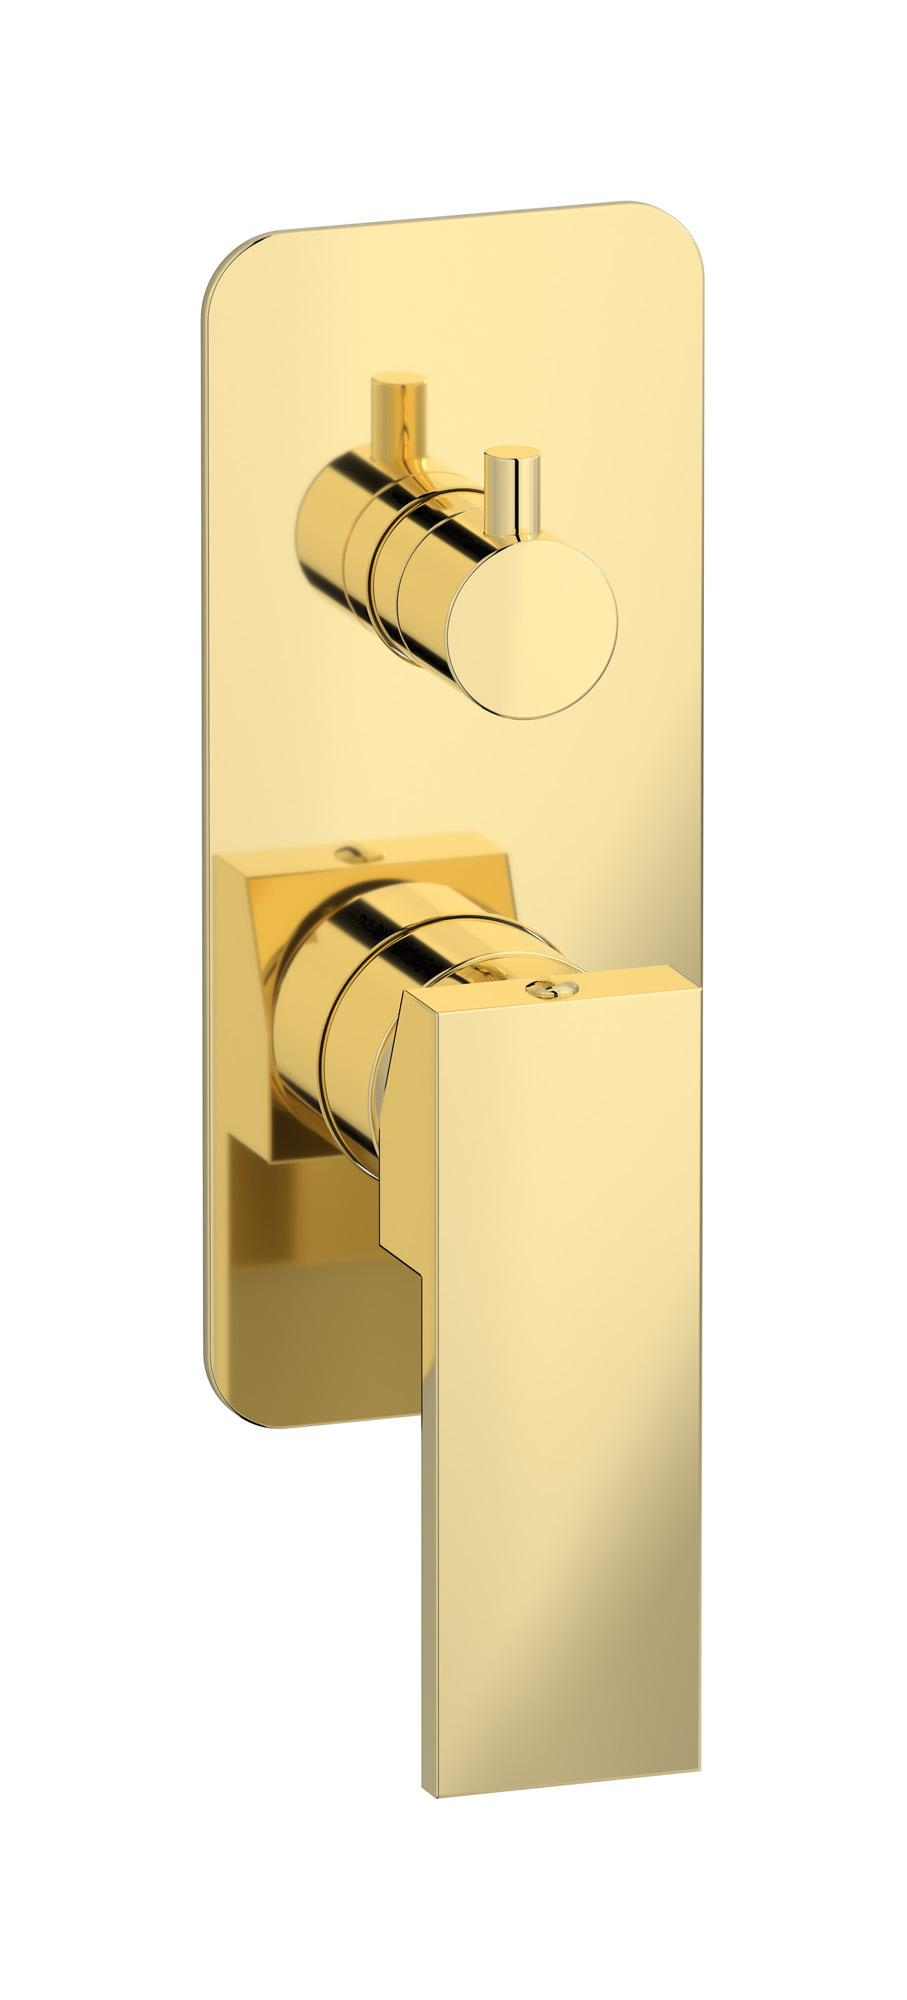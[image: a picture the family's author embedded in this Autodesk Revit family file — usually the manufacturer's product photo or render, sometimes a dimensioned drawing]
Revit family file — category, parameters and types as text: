
# Revit family: RU312
name_source: partatom
category: Apparecchi idraulici
units: mm (PartAtom-declared; Revit-internal decimal feet)

## family parameters
Basato su piano di lavoro = No
Condiviso = No
Mantieni orientamento annotazione = No
Numero OmniClass = 23.45.55.17
Punto di calcolo locali = No
Quota connettore circolare = Usa diametro
Sempre verticale = Sì
Taglio con vuoti quando caricato = No
Tipo di parte = Normale
Titolo OmniClass = Mixing Faucets

## types (12) — shared parameters
Cold water inlet = 10 mm  [stored 0.0328084 ft]
Commenti sul tipo = Exposed parts for manual wall mixer with three ways diverter
Connessione CW = No
Connessione HW = No
Connessione di scarico = No
Connessione di ventilazione = No
Descrizione = Exposed parts for manual wall mixer with three ways diverter
Hot water inlet = 10 mm  [stored 0.0328084 ft]
Produttore = IB Rubinetterie S.p.A.
URL = https://www.weareib.it
zero-valued in all types: Prospetto di default

## per-type parameters (varying)
| type | Finishes surface | Immagine tipo | Modello |
| Matt White | IB_matt white | RU312BO.jpg | RU312BO |
| Chrome | IB_Chrome | RU312CC.jpg | RU312CC |
| Black Chrome | IB_Black chrome | RU312CF.jpg | RU312CF |
| Brushed Black Chrome | IB_Brushed black chrome | RU312CS.jpg | RU312CS |
| Pale Gold | IB_Pale gold | RU312II.jpg | RU312II |
| Brushed Pale Gold | IB_brushed pale gold | RU312IS.jpg | RU312IS |
| Matt Black | IB_matt black | RU312NP.jpg | RU312NP |
| Gold | IB_gold | RU312OO.jpg | RU312OO |
| Brushed Gold | IB_brushed gold | RU312OS.jpg | RU312OS |
| Rose Gold | IB_Rose gold | RU312RS.jpg | RU312RS |
| Brushed Rose Gold | IB_Brushed rose gold | RU312SR.jpg | RU312SR |
| Brushed Nickel | IB_Brushed nickel | RU312SS.jpg | RU312SS |

note: [stored X ft] marks values corroborated as IEEE doubles in the binary element streams (Revit-internal decimal feet)
